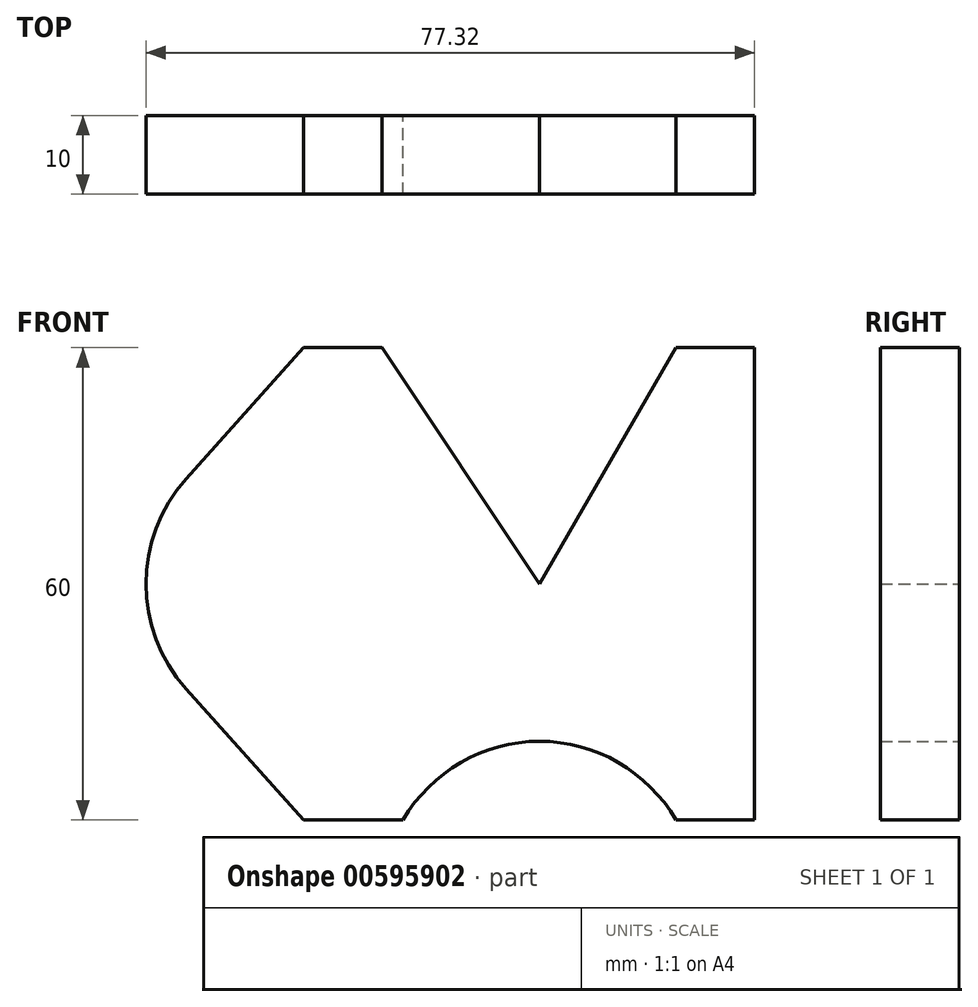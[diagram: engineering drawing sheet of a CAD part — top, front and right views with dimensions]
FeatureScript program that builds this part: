
annotation { "Feature Type Name" : "Feature", "Feature Type Description" : "" }
export const myFeature = defineFeature(function(context is Context, id is Id, definition is map)
    precondition{}
    {
        {
            var Q0;
            Q0=qCreatedBy(makeId("Front.planeOp"),FACE);
            var sketch = newSketch(context, id + "F0", { "sketchPlane" : qUnion([Q0])});
            skLineSegment(sketch, "E0", {"start": v(-20, 30) * mm, "end": v(0, 0) * mm});
            skLineSegment(sketch, "E1", {"start": v(0, 0) * mm, "end": v(17.32, 30) * mm});
            skLineSegment(sketch, "E2", {"start": v(17.32, 30) * mm, "end": v(27.32, 30) * mm});
            skLineSegment(sketch, "E3", {"start": v(27.32, 30) * mm, "end": v(27.32, -30) * mm});
            skLineSegment(sketch, "E4", {"start": v(27.32, -30) * mm, "end": v(17.32, -30) * mm});
            skLineSegment(sketch, "E5", {"start": v(-17.32, -30) * mm, "end": v(-30, -30) * mm});
            skLineSegment(sketch, "E6", {"start": v(-44.9, -13.33) * mm, "end": v(-30, -30) * mm});
            skArc(sketch, "E7", {"start": v(17.32, -30) * mm, "mid": v(0, -20) * mm, "end": v(-17.32, -30) * mm});
            skLineSegment(sketch, "E8", {"start": v(-20, 30) * mm, "end": v(-30, 30) * mm});
            skLineSegment(sketch, "E9", {"start": v(-30, 30) * mm, "end": v(-44.9, 13.33) * mm});
            skArc(sketch, "E10", {"start": v(-44.9, 13.33) * mm, "mid": v(-50, 0) * mm, "end": v(-44.9, -13.33) * mm});
            skPoint(sketch, "E11.orphan", {"position": v(-56.83, 0) * mm});
            skSolve(sketch);
        }
        {
            var Q0;
            Q0=makeQuery(id+"F0.imprint","IMPRINT",FACE,{"disambiguationData":[TD([[makeQuery(id+"F0.imprint","IMPRINT",EDGE,{"derivedFrom":sQuery(id+"F0.wireOp",EDGE,"E0")}),-1.0]])]});
            extrude(context, id + "F1", {"entities" : qUnion([Q0]), "depth" : 10 * mm, "offsetDistance" : 25 * mm});
        }
    });
